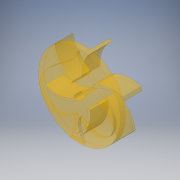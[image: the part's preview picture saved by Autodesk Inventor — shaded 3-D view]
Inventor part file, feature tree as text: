
AUTODESK INVENTOR PART (.ipt)
format: ipt  version: 2016 (Build 200138000, 138)  size: 305,664 bytes
history: native  units: mm
features: projected_geometry x8, extrude x3, other x2, sketch x1
ambient origin geometry x8: Origin, YZ Plane, XZ Plane, XY Plane, X Axis, Y Axis, Z Axis, Center Point
bodies: Body1 (feature_tree)
feature tree (14):
  other  "作業平面4"
  other  "スペード"
  extrude  "押し出し14"  Depth=5.0mm
  extrude  "押し出し15"  Depth=5.0mm
  extrude  "押し出し17"  Depth=12.0mm
  sketch  "スケッチ19"
  projected_geometry  "投影ループ30"
  projected_geometry  "投影ループ31"
  projected_geometry  "投影ループ32"
  projected_geometry  "投影ループ33"
  projected_geometry  "投影ループ34"
  projected_geometry  "投影ループ35"
  projected_geometry  "投影ループ36"
  projected_geometry  "投影ループ37"
